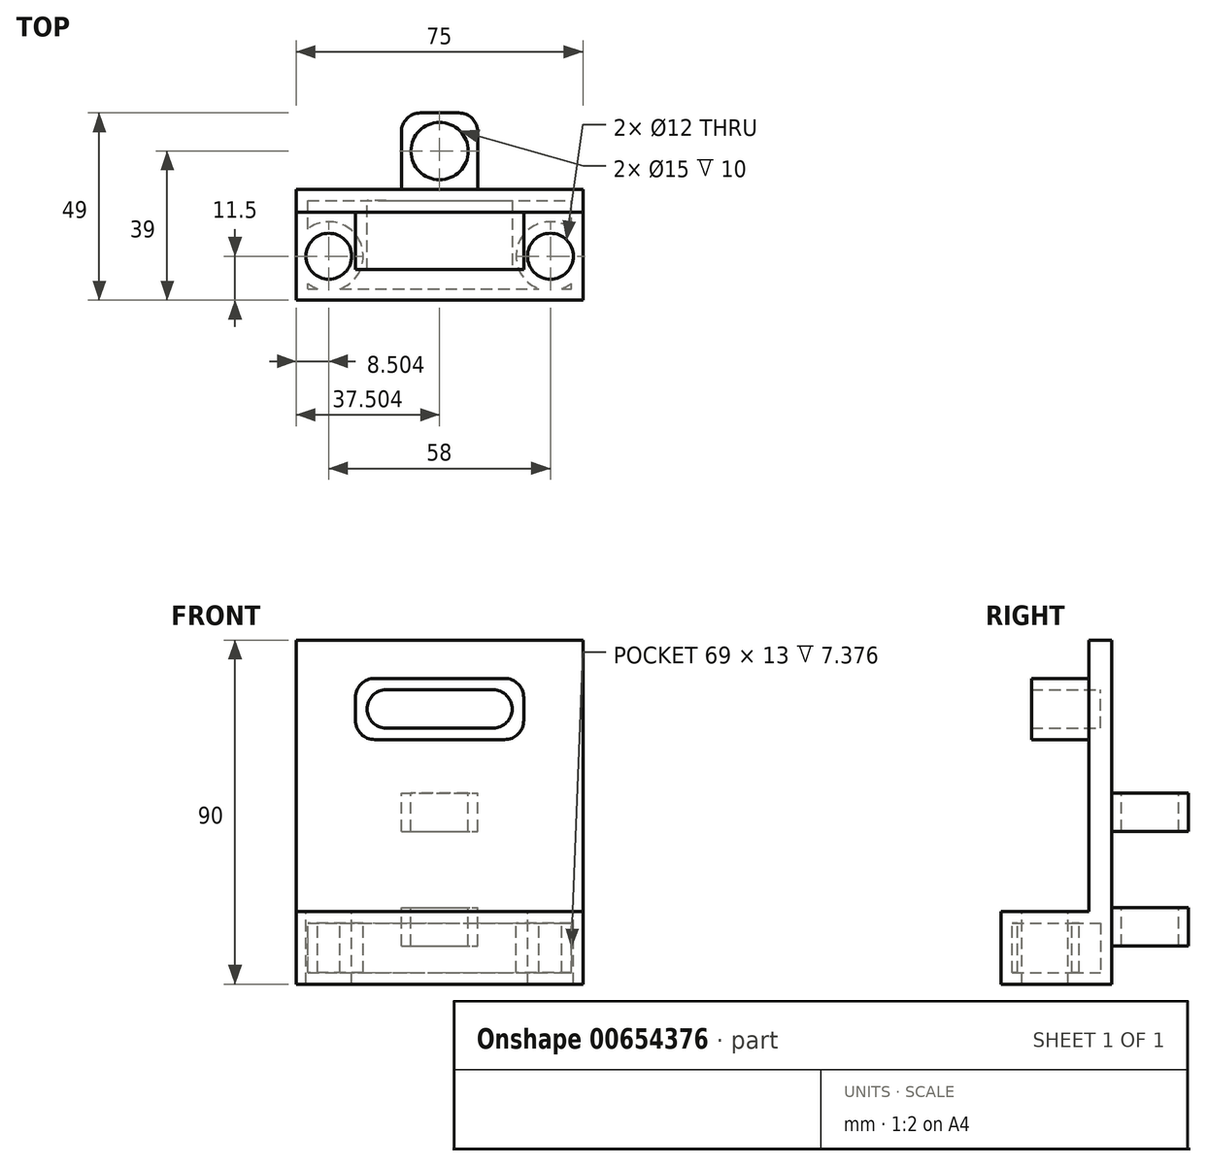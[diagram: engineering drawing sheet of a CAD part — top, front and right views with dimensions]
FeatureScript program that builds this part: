
annotation { "Feature Type Name" : "Feature", "Feature Type Description" : "" }
export const myFeature = defineFeature(function(context is Context, id is Id, definition is map)
    precondition{}
    {
        {
            assignVariable(context, id + "F0", {"name" : "bearingC", "anyValue" : 19 * mm});
        }
        {
            var Q0;
            Q0=qCreatedBy(makeId("Front.planeOp"),FACE);
            var sketch = newSketch(context, id + "F1", { "sketchPlane" : qUnion([Q0])});
            skLineSegment(sketch, "E0.bottom", {"start": v(-34.9, 33.22) * mm, "end": v(40.1, 33.22) * mm});
            skLineSegment(sketch, "E0.top", {"start": v(-34.9, -56.78) * mm, "end": v(40.1, -56.78) * mm});
            skLineSegment(sketch, "E0.left", {"start": v(-34.9, 33.22) * mm, "end": v(-34.9, -56.78) * mm});
            skLineSegment(sketch, "E0.right", {"start": v(40.1, 33.22) * mm, "end": v(40.1, -56.78) * mm});
            skLineSegment(sketch, "E1", {"start": v(2.6, 62) * mm, "end": v(2.6, -58.62) * mm, "construction": true});
            skPoint(sketch, "E1.startSnap0", {"position": v(2.6, 33.22) * mm});
            skPoint(sketch, "E1.endSnap0", {"position": v(2.6, -56.78) * mm});
            skLineSegment(sketch, "E2", {"start": v(-52.52, -11.78) * mm, "end": v(62.24, -11.78) * mm, "construction": true});
            skPoint(sketch, "E2.startSnap0", {"position": v(-34.9, -11.78) * mm});
            skPoint(sketch, "E3", {"position": v(2.6, -11.78) * mm});
            skSolve(sketch);
        }
        {
            var Q0;
            Q0=makeQuery(id+"F1.imprint","IMPRINT",FACE,{"disambiguationData":[TD([[makeQuery(id+"F1.imprint","IMPRINT",EDGE,{"derivedFrom":sQuery(id+"F1.wireOp",EDGE,"E0.bottom")}),-1.0]])]});
            extrude(context, id + "F2", {"entities" : qUnion([Q0]), "depth" : 6 * mm, "offsetDistance" : 25 * mm});
        }
        {
            var Q0;
            Q0=makeQuery(id+"F2.opExtrude","CAP_FACE",FACE,{"disambiguationData":[OSD([sQuery(id+"F1.wireOp",EDGE,"E0.bottom"),sQuery(id+"F1.wireOp",EDGE,"E0.top"),sQuery(id+"F1.wireOp",EDGE,"E0.left"),sQuery(id+"F1.wireOp",EDGE,"E0.right")])],"isStart":false});
            var sketch = newSketch(context, id + "F3", { "sketchPlane" : qUnion([Q0])});
            skLineSegment(sketch, "E4.bottom", {"start": v(-34.9, -56.78) * mm, "end": v(40.1, -56.78) * mm});
            skLineSegment(sketch, "E4.top", {"start": v(-34.9, -37.78) * mm, "end": v(40.1, -37.78) * mm});
            skLineSegment(sketch, "E4.left", {"start": v(-34.9, -56.78) * mm, "end": v(-34.9, -37.78) * mm});
            skLineSegment(sketch, "E4.right", {"start": v(40.1, -56.78) * mm, "end": v(40.1, -37.78) * mm});
            skSolve(sketch);
        }
        {
            var Q0;
            Q0=makeQuery(id+"F3.imprint","IMPRINT",FACE,{"disambiguationData":[TD([[makeQuery(id+"F3.imprint","IMPRINT",EDGE,{"derivedFrom":sQuery(id+"F3.wireOp",EDGE,"E4.bottom")}),1.0]])]});
            extrude(context, id + "F4", {"entities" : qUnion([Q0]), "operationType" : NewBodyOperationType.ADD, "depth" : getVariable(context, 'bearingC') + 2 * 2 * mm, "offsetDistance" : 25 * mm});
        }
        {
            var Q0;
            Q0=makeQuery(id+"F4.opExtrude","SWEPT_FACE",FACE,{"disambiguationData":[OSD([sQuery(id+"F3.wireOp",EDGE,"E4.top")])]});
            var sketch = newSketch(context, id + "F5", { "sketchPlane" : qUnion([Q0])});
            skCircle(sketch, "E5", {"center": v(-26.4, -17.5) * mm, "radius": 6 * mm});
            skPoint(sketch, "E5.centerSnap0", {"position": v(-34.9, -17.5) * mm});
            skCircle(sketch, "E6", {"center": v(31.6, -17.5) * mm, "radius": 6 * mm});
            skPoint(sketch, "E6.centerSnap0", {"position": v(40.1, -17.5) * mm});
            skSolve(sketch);
        }
        {
            var Q0;
            Q0=makeQuery(id+"F5.imprint","IMPRINT",FACE,{"disambiguationData":[TD([[makeQuery(id+"F5.imprint","IMPRINT",EDGE,{"derivedFrom":sQuery(id+"F5.wireOp",EDGE,"E5")}),1.0]])]});
            var Q1;
            Q1=makeQuery(id+"F5.imprint","IMPRINT",FACE,{"disambiguationData":[TD([[makeQuery(id+"F5.imprint","IMPRINT",EDGE,{"derivedFrom":sQuery(id+"F5.wireOp",EDGE,"E6")}),1.0]])]});
            var Q2;
            Q2=makeQuery(id+"F4.boolean.opBoolean","MERGE",FACE,{"derivedFrom":[makeQuery(id+"F2.opExtrude","SWEPT_FACE",FACE,{"disambiguationData":[OSD([sQuery(id+"F1.wireOp",EDGE,"E0.top")])]}),makeQuery(id+"F4.opExtrude","SWEPT_FACE",FACE,{"disambiguationData":[OSD([sQuery(id+"F3.wireOp",EDGE,"E4.bottom")])]})]});
            extrude(context, id + "F6", {"entities" : qUnion([Q0, Q1]), "operationType" : NewBodyOperationType.REMOVE, "endBound" : BoundingType.UP_TO_SURFACE, "oppositeDirection" : true, "depth" : 25 * mm, "endBoundEntityFace" : qUnion([Q2]), "offsetDistance" : 25 * mm});
        }
        {
            var Q0;
            Q0=makeQuery(id+"F2.opExtrude","CAP_FACE",FACE,{"disambiguationData":[OSD([sQuery(id+"F1.wireOp",EDGE,"E0.bottom"),sQuery(id+"F1.wireOp",EDGE,"E0.top"),sQuery(id+"F1.wireOp",EDGE,"E0.left"),sQuery(id+"F1.wireOp",EDGE,"E0.right")])],"isStart":false});
            var sketch = newSketch(context, id + "F7", { "sketchPlane" : qUnion([Q0])});
            skLineSegment(sketch, "E7.bottom", {"start": v(-19.4, 23.22) * mm, "end": v(24.6, 23.22) * mm});
            skLineSegment(sketch, "E7.top", {"start": v(-19.4, 7.22) * mm, "end": v(24.6, 7.22) * mm});
            skLineSegment(sketch, "E7.left", {"start": v(-19.4, 23.22) * mm, "end": v(-19.4, 7.22) * mm});
            skLineSegment(sketch, "E7.right", {"start": v(24.6, 23.22) * mm, "end": v(24.6, 7.22) * mm});
            skSolve(sketch);
        }
        {
            var Q0;
            Q0=makeQuery(id+"F7.imprint","IMPRINT",FACE,{"disambiguationData":[TD([[makeQuery(id+"F7.imprint","IMPRINT",EDGE,{"derivedFrom":sQuery(id+"F7.wireOp",EDGE,"E7.bottom")}),-1.0]])]});
            extrude(context, id + "F8", {"entities" : qUnion([Q0]), "operationType" : NewBodyOperationType.ADD, "depth" : 15 * mm, "offsetDistance" : 25 * mm});
        }
        {
            var Q0;
            Q0=makeQuery(id+"F8.opExtrude","CAP_FACE",FACE,{"disambiguationData":[OSD([sQuery(id+"F7.wireOp",EDGE,"E7.bottom"),sQuery(id+"F7.wireOp",EDGE,"E7.top"),sQuery(id+"F7.wireOp",EDGE,"E7.left"),sQuery(id+"F7.wireOp",EDGE,"E7.right")])],"isStart":false});
            shell(context, id + "F9", {"entities" : qUnion([Q0]), "thickness" : 3 * mm});
        }
        {
            var Q0;
            Q0=makeQuery(id+"F8.opExtrude","SWEPT_EDGE",EDGE,{"disambiguationData":[OSD([sQuery(id+"F7.wireOp",EDGE,"E7.bottom"),sQuery(id+"F7.wireOp",EDGE,"E7.left")])]});
            var Q1;
            Q1=makeQuery(id+"F9.opShell","OFFSET_EDGE",EDGE,{"disambiguationData":[OSD([sQuery(id+"F7.wireOp",EDGE,"E7.bottom"),sQuery(id+"F7.wireOp",EDGE,"E7.left")])]});
            var Q2;
            Q2=makeQuery(id+"F9.opShell","OFFSET_EDGE",EDGE,{"disambiguationData":[OSD([sQuery(id+"F7.wireOp",EDGE,"E7.top"),sQuery(id+"F7.wireOp",EDGE,"E7.left")])]});
            var Q3;
            Q3=makeQuery(id+"F8.opExtrude","SWEPT_EDGE",EDGE,{"disambiguationData":[OSD([sQuery(id+"F7.wireOp",EDGE,"E7.top"),sQuery(id+"F7.wireOp",EDGE,"E7.left")])]});
            var Q4;
            Q4=makeQuery(id+"F9.opShell","OFFSET_EDGE",EDGE,{"disambiguationData":[OSD([sQuery(id+"F7.wireOp",EDGE,"E7.bottom"),sQuery(id+"F7.wireOp",EDGE,"E7.right")])]});
            var Q5;
            Q5=makeQuery(id+"F9.opShell","OFFSET_EDGE",EDGE,{"disambiguationData":[OSD([sQuery(id+"F7.wireOp",EDGE,"E7.top"),sQuery(id+"F7.wireOp",EDGE,"E7.right")])]});
            var Q6;
            Q6=makeQuery(id+"F8.opExtrude","SWEPT_EDGE",EDGE,{"disambiguationData":[OSD([sQuery(id+"F7.wireOp",EDGE,"E7.top"),sQuery(id+"F7.wireOp",EDGE,"E7.right")])]});
            var Q7;
            Q7=makeQuery(id+"F8.opExtrude","SWEPT_EDGE",EDGE,{"disambiguationData":[OSD([sQuery(id+"F7.wireOp",EDGE,"E7.bottom"),sQuery(id+"F7.wireOp",EDGE,"E7.right")])]});
            fillet(context, id + "F10", {"entities" : qUnion([Q0, Q1, Q2, Q3, Q4, Q5, Q6, Q7]), "radius" : 5 * mm, "tangentPropagation" : true, "allowEdgeOverflow" : false});
        }
        {
            var Q0;
            Q0=makeQuery(id+"F2.opExtrude","CAP_FACE",FACE,{"disambiguationData":[OSD([sQuery(id+"F1.wireOp",EDGE,"E0.bottom"),sQuery(id+"F1.wireOp",EDGE,"E0.top"),sQuery(id+"F1.wireOp",EDGE,"E0.left"),sQuery(id+"F1.wireOp",EDGE,"E0.right")])],"isStart":true});
            var sketch = newSketch(context, id + "F11", { "sketchPlane" : qUnion([Q0])});
            skLineSegment(sketch, "E8", {"start": v(-2.6, 40.8) * mm, "end": v(-2.6, -65.38) * mm, "construction": true});
            skPoint(sketch, "E8.startSnap0", {"position": v(-2.6, 33.22) * mm});
            skLineSegment(sketch, "E9.bottom", {"start": v(7.4, -46.78) * mm, "end": v(-12.6, -46.78) * mm});
            skLineSegment(sketch, "E9.top", {"start": v(7.4, -36.78) * mm, "end": v(-12.6, -36.78) * mm});
            skLineSegment(sketch, "E9.left", {"start": v(7.4, -46.78) * mm, "end": v(7.4, -36.78) * mm});
            skLineSegment(sketch, "E9.right", {"start": v(-12.6, -46.78) * mm, "end": v(-12.6, -36.78) * mm});
            skPoint(sketch, "E9.middle", {"position": v(-2.6, -41.78) * mm});
            skLineSegment(sketch, "E10.0.1.0", {"start": v(-12.6, -16.78) * mm, "end": v(-12.6, -6.78) * mm});
            skLineSegment(sketch, "E10.0.1.1", {"start": v(7.4, -16.78) * mm, "end": v(7.4, -6.78) * mm});
            skLineSegment(sketch, "E10.0.1.2", {"start": v(7.4, -6.78) * mm, "end": v(-12.6, -6.78) * mm});
            skPoint(sketch, "E10.0.1.3", {"position": v(-2.6, -11.78) * mm});
            skLineSegment(sketch, "E10.0.1.4", {"start": v(7.4, -16.78) * mm, "end": v(-12.6, -16.78) * mm});
            skLineSegment(sketch, "E10.direction1", {"start": v(-12.6, -46.78) * mm, "end": v(12.4, -46.78) * mm, "construction": true});
            skLineSegment(sketch, "E10.direction2", {"start": v(-12.6, -46.78) * mm, "end": v(-12.6, -16.78) * mm, "construction": true});
            skSolve(sketch);
        }
        {
            var Q0;
            Q0=makeQuery(id+"F11.imprint","IMPRINT",FACE,{"disambiguationData":[TD([[makeQuery(id+"F11.imprint","IMPRINT",EDGE,{"derivedFrom":sQuery(id+"F11.wireOp",EDGE,"E10.0.1.0")}),-1.0]])]});
            var Q1;
            Q1=makeQuery(id+"F11.imprint","IMPRINT",FACE,{"disambiguationData":[TD([[makeQuery(id+"F11.imprint","IMPRINT",EDGE,{"derivedFrom":sQuery(id+"F11.wireOp",EDGE,"E9.bottom")}),-1.0]])]});
            extrude(context, id + "F12", {"entities" : qUnion([Q0, Q1]), "operationType" : NewBodyOperationType.ADD, "depth" : 20 * mm, "offsetDistance" : 25 * mm});
        }
        {
            var Q0;
            Q0=makeQuery(id+"F12.opExtrude","SWEPT_FACE",FACE,{"disambiguationData":[OSD([sQuery(id+"F11.wireOp",EDGE,"E10.0.1.2")])]});
            var sketch = newSketch(context, id + "F13", { "sketchPlane" : qUnion([Q0])});
            skCircle(sketch, "E11", {"center": v(2.6, 10) * mm, "radius": 7.5 * mm});
            skPoint(sketch, "E11.centerSnap0", {"position": v(12.6, 10) * mm});
            skPoint(sketch, "E11.centerSnap1", {"position": v(2.6, 0) * mm});
            skSolve(sketch);
        }
        {
            var Q0;
            Q0=makeQuery(id+"F13.imprint","IMPRINT",FACE,{"disambiguationData":[TD([[makeQuery(id+"F13.imprint","IMPRINT",EDGE,{"derivedFrom":sQuery(id+"F13.wireOp",EDGE,"E11")}),1.0]])]});
            var Q1;
            Q1=makeQuery(id+"F12.opExtrude","SWEPT_FACE",FACE,{"disambiguationData":[OSD([sQuery(id+"F11.wireOp",EDGE,"E9.bottom")])]});
            extrude(context, id + "F14", {"entities" : qUnion([Q0]), "operationType" : NewBodyOperationType.REMOVE, "endBound" : BoundingType.UP_TO_SURFACE, "oppositeDirection" : true, "depth" : 25 * mm, "endBoundEntityFace" : qUnion([Q1]), "offsetDistance" : 25 * mm});
        }
        {
            var Q0;
            Q0=makeQuery(id+"F12.opExtrude","CAP_EDGE",EDGE,{"disambiguationData":[OSD([sQuery(id+"F11.wireOp",EDGE,"E10.0.1.0")])],"isStart":false});
            var Q1;
            Q1=makeQuery(id+"F12.opExtrude","CAP_EDGE",EDGE,{"disambiguationData":[OSD([sQuery(id+"F11.wireOp",EDGE,"E10.0.1.1")])],"isStart":false});
            var Q2;
            Q2=makeQuery(id+"F12.opExtrude","CAP_EDGE",EDGE,{"disambiguationData":[OSD([sQuery(id+"F11.wireOp",EDGE,"E10.0.1.1")])],"isStart":true});
            var Q3;
            Q3=makeQuery(id+"F12.opExtrude","CAP_EDGE",EDGE,{"disambiguationData":[OSD([sQuery(id+"F11.wireOp",EDGE,"E10.0.1.0")])],"isStart":true});
            var Q4;
            Q4=makeQuery(id+"F12.opExtrude","CAP_EDGE",EDGE,{"disambiguationData":[OSD([sQuery(id+"F11.wireOp",EDGE,"E9.right")])],"isStart":true});
            var Q5;
            Q5=makeQuery(id+"F12.opExtrude","CAP_EDGE",EDGE,{"disambiguationData":[OSD([sQuery(id+"F11.wireOp",EDGE,"E9.right")])],"isStart":false});
            var Q6;
            Q6=makeQuery(id+"F12.opExtrude","CAP_EDGE",EDGE,{"disambiguationData":[OSD([sQuery(id+"F11.wireOp",EDGE,"E9.left")])],"isStart":true});
            var Q7;
            Q7=makeQuery(id+"F12.opExtrude","CAP_EDGE",EDGE,{"disambiguationData":[OSD([sQuery(id+"F11.wireOp",EDGE,"E9.left")])],"isStart":false});
            fillet(context, id + "F15", {"entities" : qUnion([Q0, Q1, Q2, Q3, Q4, Q5, Q6, Q7]), "radius" : 5 * mm, "tangentPropagation" : true, "allowEdgeOverflow" : false});
        }
    });
